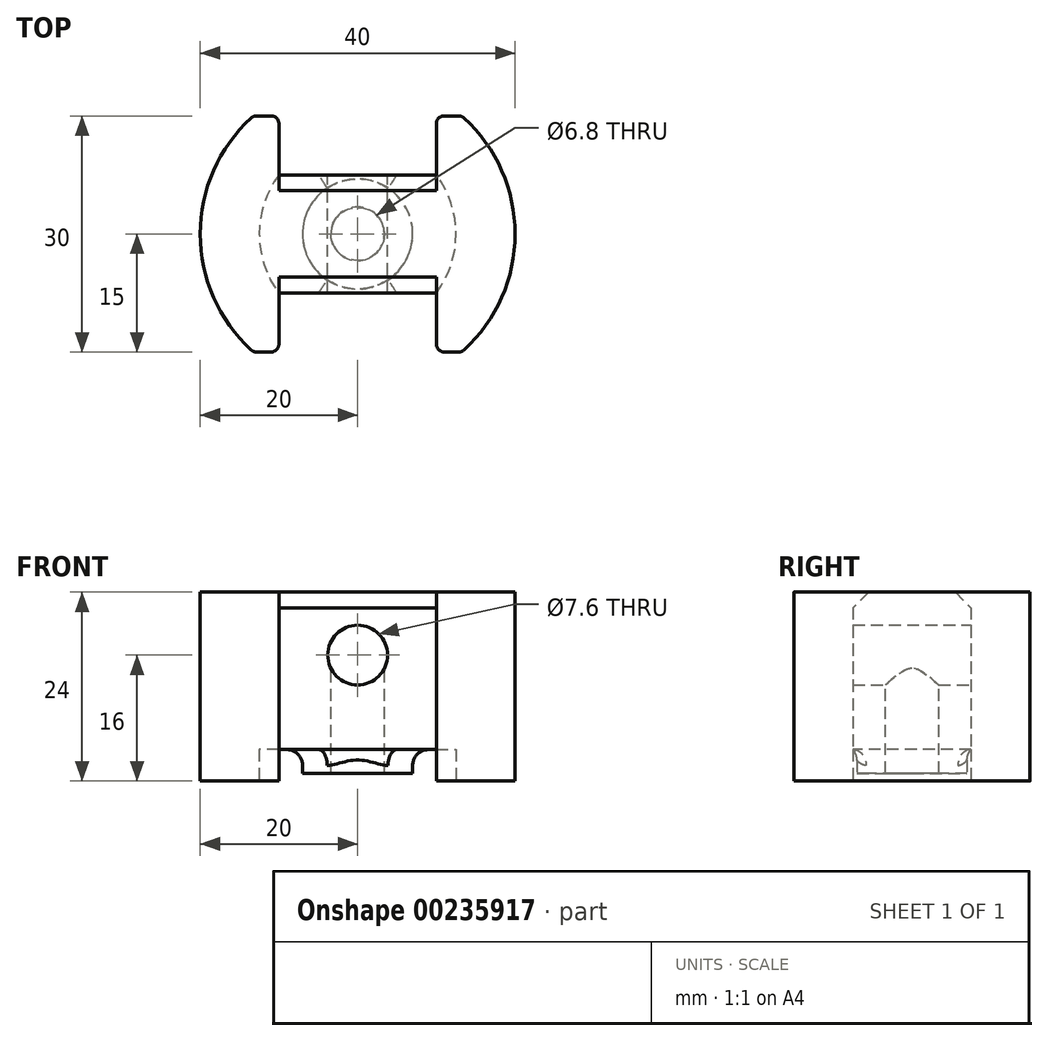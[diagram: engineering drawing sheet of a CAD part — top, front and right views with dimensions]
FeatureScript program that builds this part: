
annotation { "Feature Type Name" : "Feature", "Feature Type Description" : "" }
export const myFeature = defineFeature(function(context is Context, id is Id, definition is map)
    precondition{}
    {
        {
            var Q0;
            Q0=qCreatedBy(makeId("Top.planeOp"),FACE);
            var sketch = newSketch(context, id + "F0", { "sketchPlane" : qUnion([Q0])});
            skArc(sketch, "E0", {"start": v(13.23, -15) * mm, "mid": v(20, 0) * mm, "end": v(13.23, 15) * mm});
            skArc(sketch, "E1", {"start": v(-10, 7.5) * mm, "mid": v(-12.5, 0) * mm, "end": v(-10, -7.5) * mm});
            skLineSegment(sketch, "E2.0", {"start": v(10, 7.5) * mm, "end": v(10, 15) * mm});
            skLineSegment(sketch, "E2.1", {"start": v(10, -7.5) * mm, "end": v(10, -15) * mm});
            skLineSegment(sketch, "E3.0", {"start": v(-10, 7.5) * mm, "end": v(-10, 15) * mm});
            skLineSegment(sketch, "E3.1", {"start": v(-10, -7.5) * mm, "end": v(-10, -15) * mm});
            skArc(sketch, "E4.trimOffspring", {"start": v(-13.23, 15) * mm, "mid": v(-20, 0) * mm, "end": v(-13.23, -15) * mm});
            skArc(sketch, "E5.trimOffspring", {"start": v(10, -7.5) * mm, "mid": v(12.5, 0) * mm, "end": v(10, 7.5) * mm});
            skLineSegment(sketch, "E6", {"start": v(10, -15) * mm, "end": v(13.23, -15) * mm});
            skLineSegment(sketch, "E7", {"start": v(-10, -15) * mm, "end": v(-13.23, -15) * mm});
            skLineSegment(sketch, "E8.MirrorCS", {"start": v(-10, 15) * mm, "end": v(-13.23, 15) * mm});
            skLineSegment(sketch, "E9.MirrorCS", {"start": v(10, 15) * mm, "end": v(13.23, 15) * mm});
            skCircle(sketch, "E10", {"center": v(0, 0) * mm, "radius": 20 * mm});
            skCircle(sketch, "E11", {"center": v(0, 0) * mm, "radius": 12.5 * mm});
            skLineSegment(sketch, "E12", {"start": v(-10, 7.5) * mm, "end": v(10, 7.5) * mm});
            skLineSegment(sketch, "E13", {"start": v(10, -7.5) * mm, "end": v(-10, -7.5) * mm});
            skCircle(sketch, "E14", {"center": v(0, 0) * mm, "radius": 7 * mm});
            skSolve(sketch);
        }
        {
            var Q0;
            {var subQ3=sQuery(id+"F0.wireOp",EDGE,"E3.0");Q0=makeQuery(id+"F0.imprint","IMPRINT",FACE,{"disambiguationData":[TD([[makeQuery(id+"F0.imprint","IMPRINT",EDGE,{"derivedFrom":subQ3}),1.0]])]});}
            var Q1;
            {var subQ3=sQuery(id+"F0.wireOp",EDGE,"E2.0");Q1=makeQuery(id+"F0.imprint","IMPRINT",FACE,{"disambiguationData":[TD([[makeQuery(id+"F0.imprint","IMPRINT",EDGE,{"derivedFrom":subQ3}),-1.0]])]});}
            var Q2;
            {var subQ0=sQuery(id+"F0.wireOp",EDGE,"E12");Q2=makeQuery(id+"F0.imprint","IMPRINT",FACE,{"disambiguationData":[TD([[makeQuery(id+"F0.imprint","IMPRINT",EDGE,{"derivedFrom":subQ0}),-1.0]])]});}
            var Q3;
            Q3=makeQuery(id+"F0.imprint","IMPRINT",FACE,{"disambiguationData":[TD([[makeQuery(id+"F0.imprint","IMPRINT",EDGE,{"derivedFrom":sQuery(id+"F0.wireOp",EDGE,"E14")}),1.0]])]});
            extrude(context, id + "F1", {"entities" : qUnion([Q0, Q1, Q2, Q3]), "depth" : 24 * mm});
        }
        {
            var Q0;
            {var subQ1=sQuery(id+"F0.wireOp",EDGE,"E12");Q0=makeQuery(id+"F0.imprint","IMPRINT",FACE,{"disambiguationData":[TD([[makeQuery(id+"F0.imprint","IMPRINT",EDGE,{"derivedFrom":subQ1}),-1.0]])]});}
            extrude(context, id + "F2", {"entities" : qUnion([Q0]), "operationType" : NewBodyOperationType.REMOVE, "depth" : 4 * mm});
        }
        {
            var Q0;
            Q0=makeQuery(id+"F0.imprint","IMPRINT",FACE,{"disambiguationData":[TD([[makeQuery(id+"F0.imprint","IMPRINT",EDGE,{"derivedFrom":sQuery(id+"F0.wireOp",EDGE,"E14")}),1.0]])]});
            extrude(context, id + "F3", {"entities" : qUnion([Q0]), "operationType" : NewBodyOperationType.REMOVE, "depth" : 1 * mm});
        }
        {
            var Q0;
            Q0=makeQuery(id+"F1.opExtrude","CAP_EDGE",EDGE,{"disambiguationData":[OSD([sQuery(id+"F0.wireOp",EDGE,"E12")])],"isStart":false});
            var Q1;
            Q1=makeQuery(id+"F1.opExtrude","CAP_EDGE",EDGE,{"disambiguationData":[OSD([sQuery(id+"F0.wireOp",EDGE,"E13")])],"isStart":false});
            chamfer(context, id + "F4", {"entities" : qUnion([Q0, Q1]), "chamferType" : ChamferType.OFFSET_ANGLE, "width" : 2 * mm, "oppositeDirection" : false, "angle" : 45 * degree});
        }
        {
            var Q0;
            Q0=makeQuery(id+"F2.boolean.opBoolean","COPY",EDGE,{"derivedFrom":makeQuery(id+"F2.opExtrude","CAP_EDGE",EDGE,{"disambiguationData":[OSD([sQuery(id+"F0.wireOp",EDGE,"E14")])],"isStart":false})});
            fillet(context, id + "F5", {"entities" : qUnion([Q0]), "radius" : 2 * mm, "allowEdgeOverflow" : false});
        }
        {
            var Q0;
            Q0=makeQuery(id+"F1.opExtrude","SWEPT_EDGE",EDGE,{"disambiguationData":[OSD([sQuery(id+"F0.wireOp",EDGE,"E2.1"),sQuery(id+"F0.wireOp",EDGE,"E6")])]});
            var Q1;
            Q1=makeQuery(id+"F1.opExtrude","SWEPT_EDGE",EDGE,{"disambiguationData":[OSD([sQuery(id+"F0.wireOp",EDGE,"E3.1"),sQuery(id+"F0.wireOp",EDGE,"E7")])]});
            var Q2;
            Q2=makeQuery(id+"F1.opExtrude","SWEPT_EDGE",EDGE,{"disambiguationData":[OSD([sQuery(id+"F0.wireOp",EDGE,"E2.0"),sQuery(id+"F0.wireOp",EDGE,"E9.MirrorCS")])]});
            var Q3;
            Q3=makeQuery(id+"F1.opExtrude","SWEPT_EDGE",EDGE,{"disambiguationData":[OSD([sQuery(id+"F0.wireOp",EDGE,"E3.0"),sQuery(id+"F0.wireOp",EDGE,"E8.MirrorCS")])]});
            var Q4;
            Q4=makeQuery(id+"F1.opExtrude","SWEPT_EDGE",EDGE,{"disambiguationData":[OSD([sQuery(id+"F0.wireOp",EDGE,"E8.MirrorCS"),sQuery(id+"F0.wireOp",EDGE,"E10")])]});
            var Q5;
            Q5=makeQuery(id+"F1.opExtrude","SWEPT_EDGE",EDGE,{"disambiguationData":[OSD([sQuery(id+"F0.wireOp",EDGE,"E9.MirrorCS"),sQuery(id+"F0.wireOp",EDGE,"E10")])]});
            var Q6;
            Q6=makeQuery(id+"F1.opExtrude","SWEPT_EDGE",EDGE,{"disambiguationData":[OSD([sQuery(id+"F0.wireOp",EDGE,"E6"),sQuery(id+"F0.wireOp",EDGE,"E10")])]});
            var Q7;
            Q7=makeQuery(id+"F1.opExtrude","SWEPT_EDGE",EDGE,{"disambiguationData":[OSD([sQuery(id+"F0.wireOp",EDGE,"E7"),sQuery(id+"F0.wireOp",EDGE,"E10")])]});
            fillet(context, id + "F6", {"entities" : qUnion([Q0, Q1, Q2, Q3, Q4, Q5, Q6, Q7]), "radius" : 1 * mm, "tangentPropagation" : true, "allowEdgeOverflow" : false});
        }
        {
            var Q0;
            Q0=qCreatedBy(makeId("Front.planeOp"),FACE);
            cPlane(context, id + "F7", {"entities" : qUnion([Q0]), "cplaneType" : CPlaneType.OFFSET, "offset" : 7.5 * mm, "width" : 150 * mm, "height" : 150 * mm});
        }
        {
            var Q0;
            Q0=qCreatedBy(id+"F7.planeOp",FACE);
            var sketch = newSketch(context, id + "F8", { "sketchPlane" : qUnion([Q0])});
            skLineSegment(sketch, "E15", {"start": v(0, 0) * mm, "end": v(0, 16) * mm});
            skSolve(sketch);
        }
        {
            var Q0;
            Q0=sQuery(id+"F8.wireOp",VERTEX,"E15.end");
            var Q1;
            Q1=makeQuery(id+"F1.opExtrude","SWEPT_BODY",BODY,{"disambiguationData":[OSD([sQuery(id+"F0.wireOp",EDGE,"E2.0"),sQuery(id+"F0.wireOp",EDGE,"E2.1"),sQuery(id+"F0.wireOp",EDGE,"E3.0"),sQuery(id+"F0.wireOp",EDGE,"E3.1"),sQuery(id+"F0.wireOp",EDGE,"E6"),sQuery(id+"F0.wireOp",EDGE,"E7"),sQuery(id+"F0.wireOp",EDGE,"E8.MirrorCS"),sQuery(id+"F0.wireOp",EDGE,"E9.MirrorCS"),sQuery(id+"F0.wireOp",EDGE,"E10"),sQuery(id+"F0.wireOp",EDGE,"E12"),sQuery(id+"F0.wireOp",EDGE,"E13")])]});
            hole(context, id + "F9", {"style" : HoleStyle.SIMPLE, "endStyle" : HoleEndStyle.THROUGH, "standardTappedOrClearance" : lookupTablePath({ "standard" : "ISO", "size" : "7.6", "type" : "Drilled" }), "standardBlindInLast" : lookupTablePath({ "standard" : "ISO", "size" : "7.6", "type" : "Drilled" }), "holeDiameter" : 7.6 * mm, "isTappedThrough" : true, "tappedDepth" : 3.5 * mm, "tapClearance" : 3, "startFromSketch" : true, "locations" : qUnion([Q0]), "scope" : qUnion([Q1])});
        }
        {
            var Q0;
            Q0=sQuery(id+"F0.wireOp",VERTEX,"E10.center");
            var Q1;
            Q1=makeQuery(id+"F1.opExtrude","SWEPT_BODY",BODY,{"disambiguationData":[OSD([sQuery(id+"F0.wireOp",EDGE,"E2.0"),sQuery(id+"F0.wireOp",EDGE,"E2.1"),sQuery(id+"F0.wireOp",EDGE,"E3.0"),sQuery(id+"F0.wireOp",EDGE,"E3.1"),sQuery(id+"F0.wireOp",EDGE,"E6"),sQuery(id+"F0.wireOp",EDGE,"E7"),sQuery(id+"F0.wireOp",EDGE,"E8.MirrorCS"),sQuery(id+"F0.wireOp",EDGE,"E9.MirrorCS"),sQuery(id+"F0.wireOp",EDGE,"E10"),sQuery(id+"F0.wireOp",EDGE,"E12"),sQuery(id+"F0.wireOp",EDGE,"E13")])]});
            hole(context, id + "F10", {"style" : HoleStyle.SIMPLE, "endStyle" : HoleEndStyle.BLIND, "oppositeDirection" : true, "standardTappedOrClearance" : lookupTablePath({ "standard" : "ISO", "engagement" : "75%", "pitch" : "1.25 mm", "size" : "M8", "type" : "Tapped" }), "standardBlindInLast" : lookupTablePath({ "standard" : "ISO", "engagement" : "75%", "pitch" : "1.25 mm", "size" : "M8", "type" : "Tapped" }), "holeDiameter" : 6.8 * mm, "showTappedDepth" : true, "holeDepth" : 17 * mm, "tappedDepth" : 13.25 * mm, "tapClearance" : 3, "startFromSketch" : true, "locations" : qUnion([Q0]), "scope" : qUnion([Q1]), "majorDiameter" : 8 * mm});
        }
    });
